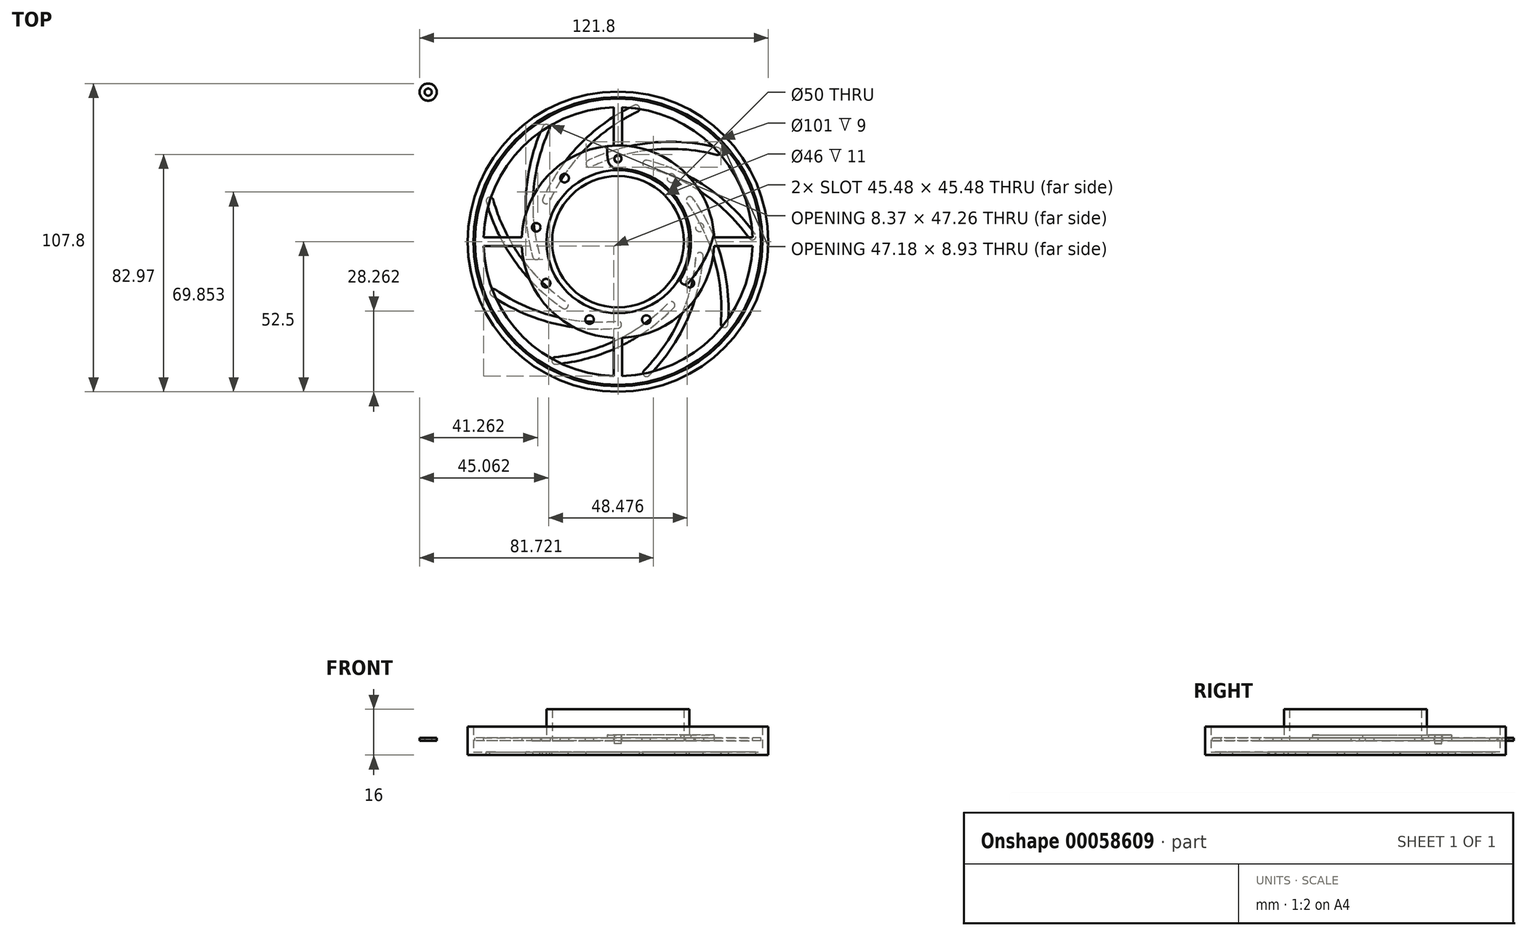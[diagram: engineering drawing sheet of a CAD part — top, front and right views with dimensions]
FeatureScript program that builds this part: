
annotation { "Feature Type Name" : "Feature", "Feature Type Description" : "" }
export const myFeature = defineFeature(function(context is Context, id is Id, definition is map)
    precondition{}
    {
        {
            var Q0;
            Q0=qCreatedBy(makeId("Top.planeOp"),FACE);
            var sketch = newSketch(context, id + "F0", { "sketchPlane" : qUnion([Q0])});
            skCircle(sketch, "E0", {"center": v(0, 0) * mm, "radius": 50 * mm});
            skCircle(sketch, "E1", {"center": v(0, 0) * mm, "radius": 25 * mm});
            skSolve(sketch);
        }
        {
            var Q0;
            Q0 = qSketchRegion(id + "F0", true);
            extrude(context, id + "F1", {"entities" : qUnion([Q0]), "depth" : 1 * mm});
        }
        {
            var Q0;
            Q0=makeQuery(id+"F1.opExtrude","CAP_FACE",FACE,{"disambiguationData":[OSD([sQuery(id+"F0.wireOp",EDGE,"E0"),sQuery(id+"F0.wireOp",EDGE,"E1")])],"isStart":false});
            var sketch = newSketch(context, id + "F2", { "sketchPlane" : qUnion([Q0])});
            skCircle(sketch, "E2", {"center": v(0, 29) * mm, "radius": 1.5 * mm});
            skSolve(sketch);
        }
        {
            var Q0;
            Q0 = qSketchRegion(id + "F2", true);
            extrude(context, id + "F3", {"entities" : qUnion([Q0]), "oppositeDirection" : true, "depth" : 5 * mm});
        }
        {
            var Q0;
            Q0=makeQuery(id+"F1.opExtrude","CAP_FACE",FACE,{"disambiguationData":[OSD([sQuery(id+"F0.wireOp",EDGE,"E0"),sQuery(id+"F0.wireOp",EDGE,"E1")])],"isStart":false});
            var sketch = newSketch(context, id + "F4", { "sketchPlane" : qUnion([Q0])});
            skArc(sketch, "E3", {"start": v(22.08, -12.75) * mm, "mid": v(22.08, 12.75) * mm, "end": v(0, 25.5) * mm});
            skCircle(sketch, "E4", {"center": v(0, 29) * mm, "radius": 1.25 * mm});
            skCircle(sketch, "E5", {"center": v(10, 45.92) * mm, "radius": 1.5 * mm, "construction": true});
            skArc(sketch, "E6", {"start": v(-3.42, 28.27) * mm, "mid": v(-2.2, 26.28) * mm, "end": v(0, 25.5) * mm});
            skArc(sketch, "E7", {"start": v(11.24, 48.66) * mm, "mid": v(10.25, 48.91) * mm, "end": v(9.24, 48.82) * mm});
            skArc(sketch, "E8", {"start": v(22.08, -12.75) * mm, "mid": v(22.5, -14.71) * mm, "end": v(24.5, -14.5) * mm});
            skLineSegment(sketch, "E9", {"start": v(0, 29) * mm, "end": v(0, 0) * mm, "construction": true});
            skLineSegment(sketch, "E10", {"start": v(0, 0) * mm, "end": v(23.38, -13.5) * mm, "construction": true});
            skPoint(sketch, "E11.first.point", {"position": v(8.68, 48.62) * mm});
            skPoint(sketch, "E11.second.point", {"position": v(23.38, -15) * mm});
            skPoint(sketch, "E11.third.point", {"position": v(-10.1, 19.77) * mm});
            skArc(sketch, "E12", {"start": v(24.5, -14.5) * mm, "mid": v(33.88, 20.44) * mm, "end": v(11.24, 48.66) * mm});
            skArc(sketch, "E13", {"start": v(9.24, 48.82) * mm, "mid": v(-1.2, 41.08) * mm, "end": v(-3.42, 28.27) * mm});
            skSolve(sketch);
        }
        {
            var Q0;
            Q0 = qSketchRegion(id + "F4", true);
            var Q1;
            Q1 = qConstructionFilter(qBodyType(qCreatedBy(id + "F4" ,EDGE), BodyType.WIRE), ConstructionObject.NO);
            extrude(context, id + "F5", {"entities" : qUnion([Q0]), "surfaceEntities" : qUnion([Q1]), "depth" : 1 * mm});
        }
        {
            var Q0;
            Q0=makeQuery(id+"F5.opExtrude","CAP_FACE",FACE,{"disambiguationData":[OSD([sQuery(id+"F4.wireOp",EDGE,"E3"),sQuery(id+"F4.wireOp",EDGE,"E4"),sQuery(id+"F4.wireOp",EDGE,"E6"),sQuery(id+"F4.wireOp",EDGE,"E7"),sQuery(id+"F4.wireOp",EDGE,"E8"),sQuery(id+"F4.wireOp",EDGE,"E12"),sQuery(id+"F4.wireOp",EDGE,"E13")])],"isStart":false});
            var sketch = newSketch(context, id + "F6", { "sketchPlane" : qUnion([Q0])});
            skCircle(sketch, "E14", {"center": v(10, 45.92) * mm, "radius": 1 * mm});
            skPoint(sketch, "E14.centerSnap0", {"position": v(10.25, 48.91) * mm});
            skSolve(sketch);
        }
        {
            var Q0;
            Q0 = qSketchRegion(id + "F6", true);
            extrude(context, id + "F7", {"entities" : qUnion([Q0]), "operationType" : NewBodyOperationType.ADD, "depth" : 7 * mm});
        }
        {
            var Q0;
            Q0=makeQuery(id+"F3.opExtrude","CAP_FACE",FACE,{"disambiguationData":[OSD([sQuery(id+"F2.wireOp",EDGE,"E2")])],"isStart":false});
            var sketch = newSketch(context, id + "F8", { "sketchPlane" : qUnion([Q0])});
            skCircle(sketch, "E15", {"center": v(0, 0) * mm, "radius": 50.5 * mm});
            skCircle(sketch, "E16", {"center": v(0, 0) * mm, "radius": 25 * mm});
            skSolve(sketch);
        }
        {
            var Q0;
            Q0 = qSketchRegion(id + "F8", true);
            extrude(context, id + "F9", {"entities" : qUnion([Q0]), "depth" : 1 * mm});
        }
        {
            var Q0;
            Q0=makeQuery(id+"F9.opExtrude","CAP_FACE",FACE,{"disambiguationData":[OSD([sQuery(id+"F8.wireOp",EDGE,"E15"),sQuery(id+"F8.wireOp",EDGE,"E16")])],"isStart":true});
            var sketch = newSketch(context, id + "F10", { "sketchPlane" : qUnion([Q0])});
            skArc(sketch, "E17.2.0", {"start": v(29.8, -5.13) * mm, "mid": v(28.66, -3.79) * mm, "end": v(27.31, -4.94) * mm});
            skPoint(sketch, "E17.center", {"position": v(0, 0) * mm});
            skArc(sketch, "E18", {"start": v(9.1, -45.05) * mm, "mid": v(9.13, -46.82) * mm, "end": v(10.9, -46.8) * mm});
            skArc(sketch, "E19", {"start": v(10.9, -46.8) * mm, "mid": v(24.02, -27.63) * mm, "end": v(29.8, -5.13) * mm});
            skArc(sketch, "E20", {"start": v(9.1, -45.05) * mm, "mid": v(21.75, -26.6) * mm, "end": v(27.31, -4.94) * mm});
            skSolve(sketch);
        }
        {
            var Q0;
            Q0 = qSketchRegion(id + "F10", true);
            extrude(context, id + "F11", {"entities" : qUnion([Q0]), "oppositeDirection" : true, "depth" : 1 * mm});
        }
        {
            var Q0;
            Q0=makeQuery(id+"F11.opExtrude","SWEPT_BODY",BODY,{"disambiguationData":[OSD([sQuery(id+"F10.wireOp",EDGE,"E17.2.0"),sQuery(id+"F10.wireOp",EDGE,"E18"),sQuery(id+"F10.wireOp",EDGE,"E19"),sQuery(id+"F10.wireOp",EDGE,"E20")])]});
            var Q1;
            Q1=makeQuery(id+"F9.opExtrude","CAP_EDGE",EDGE,{"disambiguationData":[OSD([sQuery(id+"F8.wireOp",EDGE,"E15")])],"isStart":true});
            circularPattern(context, id + "F12", {"operationType" : NewBodyOperationType.REMOVE, "entities" : qUnion([Q0]), "axis" : qUnion([Q1]), "angle" : 360 * degree, "instanceCount" : 9, "equalSpace" : true});
        }
        {
            var Q0;
            Q0=makeQuery(id+"F3.opExtrude","SWEPT_BODY",BODY,{"disambiguationData":[OSD([sQuery(id+"F2.wireOp",EDGE,"E2")])]});
            var Q1;
            Q1=makeQuery(id+"F1.opExtrude","CAP_EDGE",EDGE,{"disambiguationData":[OSD([sQuery(id+"F0.wireOp",EDGE,"E0")])],"isStart":false});
            circularPattern(context, id + "F13", {"operationType" : NewBodyOperationType.REMOVE, "entities" : qUnion([Q0]), "axis" : qUnion([Q1]), "angle" : 360 * degree, "instanceCount" : 9, "equalSpace" : true});
        }
        {
            var Q0;
            Q0=makeQuery(id+"F1.opExtrude","CAP_FACE",FACE,{"disambiguationData":[OSD([sQuery(id+"F0.wireOp",EDGE,"E0"),sQuery(id+"F0.wireOp",EDGE,"E1")])],"isStart":true});
            var sketch = newSketch(context, id + "F14", { "sketchPlane" : qUnion([Q0])});
            skCircle(sketch, "E21", {"center": v(0, 0) * mm, "radius": 33.63 * mm});
            skCircle(sketch, "E22", {"center": v(0, 0) * mm, "radius": 62.98 * mm});
            skSolve(sketch);
        }
        {
            var Q0;
            Q0 = qSketchRegion(id + "F14", true);
            extrude(context, id + "F15", {"entities" : qUnion([Q0]), "operationType" : NewBodyOperationType.REMOVE, "oppositeDirection" : true, "depth" : 25 * mm});
        }
        {
            var Q0;
            Q0=makeQuery(id+"F5.opExtrude","CAP_FACE",FACE,{"disambiguationData":[OSD([sQuery(id+"F4.wireOp",EDGE,"E3"),sQuery(id+"F4.wireOp",EDGE,"E4"),sQuery(id+"F4.wireOp",EDGE,"E6"),sQuery(id+"F4.wireOp",EDGE,"E7"),sQuery(id+"F4.wireOp",EDGE,"E8"),sQuery(id+"F4.wireOp",EDGE,"E12"),sQuery(id+"F4.wireOp",EDGE,"E13")])],"isStart":false});
            var sketch = newSketch(context, id + "F16", { "sketchPlane" : qUnion([Q0])});
            skCircle(sketch, "E23", {"center": v(0, 29) * mm, "radius": 1.2 * mm});
            skSolve(sketch);
        }
        {
            var Q0;
            Q0 = qSketchRegion(id + "F16", true);
            extrude(context, id + "F17", {"entities" : qUnion([Q0]), "oppositeDirection" : true, "depth" : 3 * mm});
        }
        {
            var Q0;
            Q0=makeQuery(id+"F9.opExtrude","CAP_FACE",FACE,{"disambiguationData":[OSD([sQuery(id+"F8.wireOp",EDGE,"E15"),sQuery(id+"F8.wireOp",EDGE,"E16")])],"isStart":false});
            var sketch = newSketch(context, id + "F18", { "sketchPlane" : qUnion([Q0])});
            skCircle(sketch, "E24", {"center": v(0, 0) * mm, "radius": 50.5 * mm});
            skCircle(sketch, "E25", {"center": v(0, 0) * mm, "radius": 52.5 * mm});
            skSolve(sketch);
        }
        {
            var Q0;
            Q0 = qSketchRegion(id + "F18", true);
            extrude(context, id + "F19", {"entities" : qUnion([Q0]), "operationType" : NewBodyOperationType.ADD, "oppositeDirection" : true, "depth" : 10 * mm});
        }
        {
            var Q0;
            Q0=makeQuery(id+"F1.opExtrude","CAP_FACE",FACE,{"disambiguationData":[OSD([sQuery(id+"F0.wireOp",EDGE,"E0"),sQuery(id+"F0.wireOp",EDGE,"E1")])],"isStart":false});
            var sketch = newSketch(context, id + "F20", { "sketchPlane" : qUnion([Q0])});
            skLineSegment(sketch, "E26.rect.bottom", {"start": v(1.5, -33) * mm, "end": v(-1.5, -33) * mm});
            skLineSegment(sketch, "E26.rect.top", {"start": v(1.5, -49.14) * mm, "end": v(-1.5, -49.14) * mm});
            skLineSegment(sketch, "E26.rect.left", {"start": v(1.5, -33) * mm, "end": v(1.5, -49.14) * mm});
            skLineSegment(sketch, "E26.rect.right", {"start": v(-1.5, -33) * mm, "end": v(-1.5, -49.14) * mm});
            skPoint(sketch, "E26.rect.middle", {"position": v(0, -41.07) * mm});
            skPoint(sketch, "E27.1.0", {"position": v(41.07, 0) * mm});
            skLineSegment(sketch, "E27.1.1", {"start": v(33, -1.5) * mm, "end": v(49.14, -1.5) * mm});
            skLineSegment(sketch, "E27.1.2", {"start": v(33, 1.5) * mm, "end": v(49.14, 1.5) * mm});
            skLineSegment(sketch, "E27.1.3", {"start": v(49.14, 1.5) * mm, "end": v(49.14, -1.5) * mm});
            skLineSegment(sketch, "E27.1.4", {"start": v(33, 1.5) * mm, "end": v(33, -1.5) * mm});
            skPoint(sketch, "E27.2.0", {"position": v(0, 41.07) * mm});
            skLineSegment(sketch, "E27.2.1", {"start": v(1.5, 33) * mm, "end": v(1.5, 49.14) * mm});
            skLineSegment(sketch, "E27.2.2", {"start": v(-1.5, 33) * mm, "end": v(-1.5, 49.14) * mm});
            skLineSegment(sketch, "E27.2.3", {"start": v(-1.5, 49.14) * mm, "end": v(1.5, 49.14) * mm});
            skLineSegment(sketch, "E27.2.4", {"start": v(-1.5, 33) * mm, "end": v(1.5, 33) * mm});
            skPoint(sketch, "E27.3.0", {"position": v(-41.07, 0) * mm});
            skLineSegment(sketch, "E27.3.1", {"start": v(-33, 1.5) * mm, "end": v(-49.14, 1.5) * mm});
            skLineSegment(sketch, "E27.3.2", {"start": v(-33, -1.5) * mm, "end": v(-49.14, -1.5) * mm});
            skLineSegment(sketch, "E27.3.3", {"start": v(-49.14, -1.5) * mm, "end": v(-49.14, 1.5) * mm});
            skLineSegment(sketch, "E27.3.4", {"start": v(-33, -1.5) * mm, "end": v(-33, 1.5) * mm});
            skPoint(sketch, "E27.center", {"position": v(0, 0) * mm});
            skSolve(sketch);
        }
        {
            var Q0;
            Q0 = qSketchRegion(id + "F20", true);
            extrude(context, id + "F21", {"entities" : qUnion([Q0]), "operationType" : NewBodyOperationType.ADD, "oppositeDirection" : true, "depth" : 1 * mm});
        }
        {
            var Q0;
            Q0=makeQuery(id+"F21.boolean.opBoolean","MERGE",FACE,{"derivedFrom":[makeQuery(id+"F1.opExtrude","CAP_FACE",FACE,{"disambiguationData":[OSD([sQuery(id+"F0.wireOp",EDGE,"E0"),sQuery(id+"F0.wireOp",EDGE,"E1")])],"isStart":false}),makeQuery(id+"F21.opExtrude","CAP_FACE",FACE,{"disambiguationData":[OSD([sQuery(id+"F20.wireOp",EDGE,"E26.rect.bottom"),sQuery(id+"F20.wireOp",EDGE,"E26.rect.top"),sQuery(id+"F20.wireOp",EDGE,"E26.rect.left"),sQuery(id+"F20.wireOp",EDGE,"E26.rect.right")])],"isStart":true}),makeQuery(id+"F21.opExtrude","CAP_FACE",FACE,{"disambiguationData":[OSD([sQuery(id+"F20.wireOp",EDGE,"E27.1.1"),sQuery(id+"F20.wireOp",EDGE,"E27.1.2"),sQuery(id+"F20.wireOp",EDGE,"E27.1.3"),sQuery(id+"F20.wireOp",EDGE,"E27.1.4")])],"isStart":true}),makeQuery(id+"F21.opExtrude","CAP_FACE",FACE,{"disambiguationData":[OSD([sQuery(id+"F20.wireOp",EDGE,"E27.2.1"),sQuery(id+"F20.wireOp",EDGE,"E27.2.2"),sQuery(id+"F20.wireOp",EDGE,"E27.2.3"),sQuery(id+"F20.wireOp",EDGE,"E27.2.4")])],"isStart":true}),makeQuery(id+"F21.opExtrude","CAP_FACE",FACE,{"disambiguationData":[OSD([sQuery(id+"F20.wireOp",EDGE,"E27.3.1"),sQuery(id+"F20.wireOp",EDGE,"E27.3.2"),sQuery(id+"F20.wireOp",EDGE,"E27.3.3"),sQuery(id+"F20.wireOp",EDGE,"E27.3.4")])],"isStart":true})]});
            var sketch = newSketch(context, id + "F22", { "sketchPlane" : qUnion([Q0])});
            skCircle(sketch, "E28", {"center": v(0, 0) * mm, "radius": 50 * mm});
            skCircle(sketch, "E29", {"center": v(0, 0) * mm, "radius": 47 * mm});
            skSolve(sketch);
        }
        {
            var Q0;
            Q0 = qSketchRegion(id + "F22", true);
            extrude(context, id + "F23", {"entities" : qUnion([Q0]), "operationType" : NewBodyOperationType.ADD, "oppositeDirection" : true, "depth" : 1 * mm});
        }
        {
            var Q0;
            Q0=makeQuery(id+"F23.boolean.opBoolean","MERGE",FACE,{"derivedFrom":[makeQuery(id+"F21.boolean.opBoolean","MERGE",FACE,{"derivedFrom":[makeQuery(id+"F1.opExtrude","CAP_FACE",FACE,{"disambiguationData":[OSD([sQuery(id+"F0.wireOp",EDGE,"E0"),sQuery(id+"F0.wireOp",EDGE,"E1")])],"isStart":true}),makeQuery(id+"F21.opExtrude","CAP_FACE",FACE,{"disambiguationData":[OSD([sQuery(id+"F20.wireOp",EDGE,"E26.rect.bottom"),sQuery(id+"F20.wireOp",EDGE,"E26.rect.top"),sQuery(id+"F20.wireOp",EDGE,"E26.rect.left"),sQuery(id+"F20.wireOp",EDGE,"E26.rect.right")])],"isStart":false}),makeQuery(id+"F21.opExtrude","CAP_FACE",FACE,{"disambiguationData":[OSD([sQuery(id+"F20.wireOp",EDGE,"E27.1.1"),sQuery(id+"F20.wireOp",EDGE,"E27.1.2"),sQuery(id+"F20.wireOp",EDGE,"E27.1.3"),sQuery(id+"F20.wireOp",EDGE,"E27.1.4")])],"isStart":false}),makeQuery(id+"F21.opExtrude","CAP_FACE",FACE,{"disambiguationData":[OSD([sQuery(id+"F20.wireOp",EDGE,"E27.2.1"),sQuery(id+"F20.wireOp",EDGE,"E27.2.2"),sQuery(id+"F20.wireOp",EDGE,"E27.2.3"),sQuery(id+"F20.wireOp",EDGE,"E27.2.4")])],"isStart":false}),makeQuery(id+"F21.opExtrude","CAP_FACE",FACE,{"disambiguationData":[OSD([sQuery(id+"F20.wireOp",EDGE,"E27.3.1"),sQuery(id+"F20.wireOp",EDGE,"E27.3.2"),sQuery(id+"F20.wireOp",EDGE,"E27.3.3"),sQuery(id+"F20.wireOp",EDGE,"E27.3.4")])],"isStart":false})]}),makeQuery(id+"F23.opExtrude","CAP_FACE",FACE,{"disambiguationData":[OSD([sQuery(id+"F22.wireOp",EDGE,"E28"),sQuery(id+"F22.wireOp",EDGE,"E29")])],"isStart":false})]});
            var sketch = newSketch(context, id + "F24", { "sketchPlane" : qUnion([Q0])});
            skCircle(sketch, "E30", {"center": v(0, 0) * mm, "radius": 25 * mm});
            skCircle(sketch, "E31", {"center": v(0, 0) * mm, "radius": 23 * mm});
            skSolve(sketch);
        }
        {
            var Q0;
            Q0 = qSketchRegion(id + "F24", true);
            extrude(context, id + "F25", {"entities" : qUnion([Q0]), "operationType" : NewBodyOperationType.ADD, "oppositeDirection" : true, "depth" : 11 * mm});
        }
        {
            var Q0;
            Q0=qCreatedBy(makeId("Top.planeOp"),FACE);
            var sketch = newSketch(context, id + "F26", { "sketchPlane" : qUnion([Q0])});
            skCircle(sketch, "E32", {"center": v(-66.3, 52.3) * mm, "radius": 1.25 * mm});
            skCircle(sketch, "E33", {"center": v(-66.3, 52.3) * mm, "radius": 3 * mm});
            skSolve(sketch);
        }
        {
            var Q0;
            Q0 = qSketchRegion(id + "F26", true);
            extrude(context, id + "F27", {"entities" : qUnion([Q0]), "depth" : 1 * mm});
        }
    });
